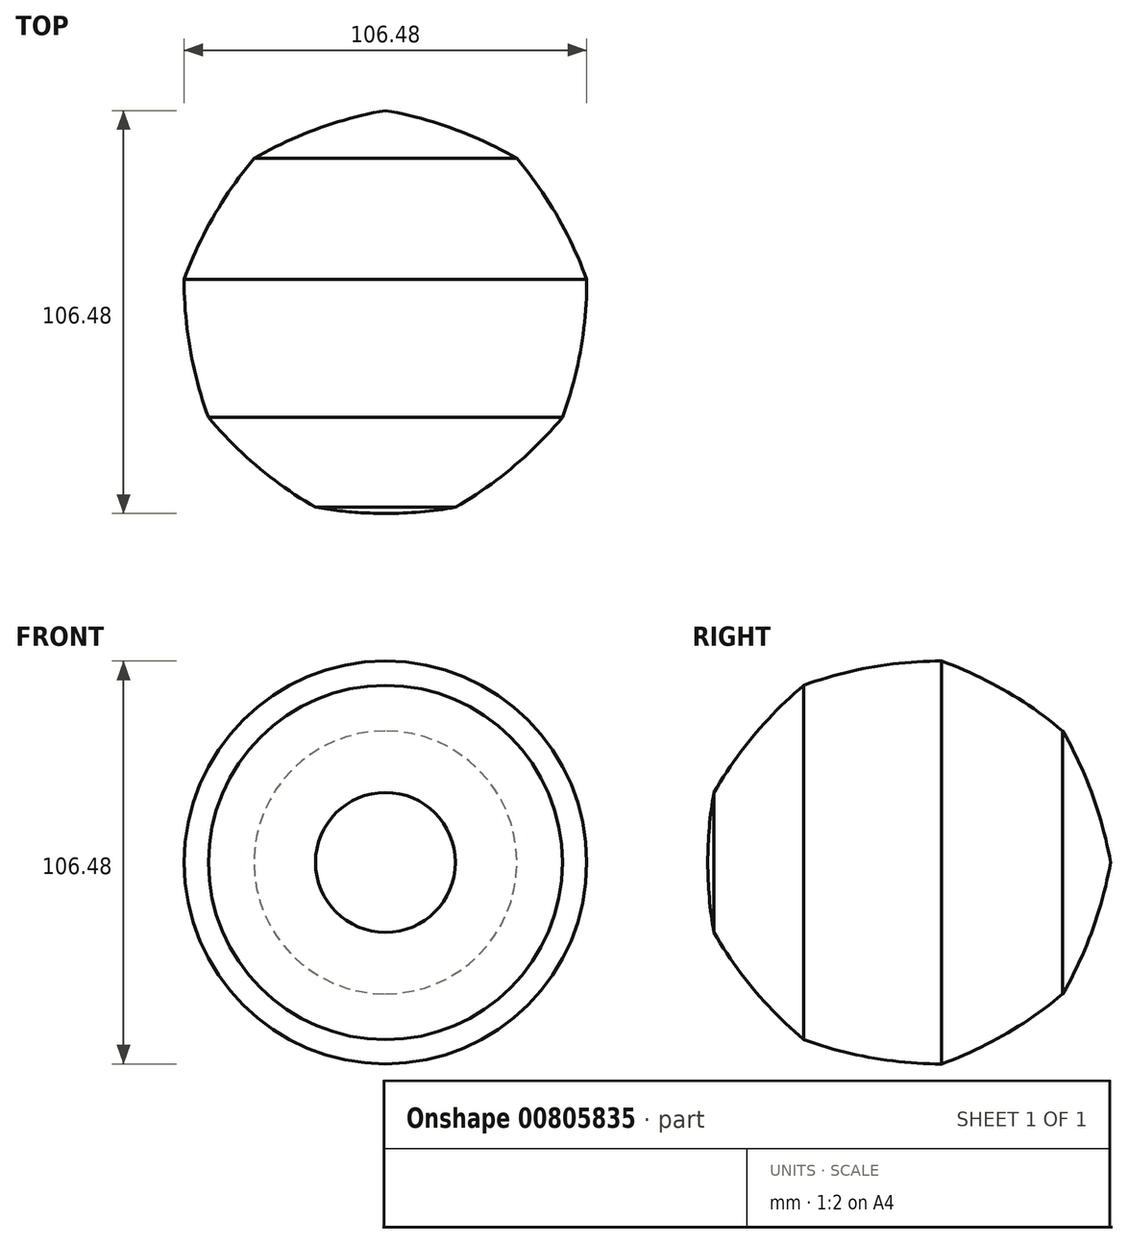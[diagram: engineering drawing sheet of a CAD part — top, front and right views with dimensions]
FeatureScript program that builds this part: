
annotation { "Feature Type Name" : "Feature", "Feature Type Description" : "" }
export const myFeature = defineFeature(function(context is Context, id is Id, definition is map)
    precondition{}
    {
        {
            var Q0;
            Q0=qCreatedBy(makeId("Top.planeOp"),FACE);
            var sketch = newSketch(context, id + "F0", { "sketchPlane" : qUnion([Q0])});
            skCircle(sketch, "E0.cCircle", {"center": v(0, 0) * mm, "radius": 50.8 * mm, "construction": true});
            skLineSegment(sketch, "E0.0", {"start": v(34.75, 41.41) * mm, "end": v(53.24, 9.39) * mm});
            skLineSegment(sketch, "E0.1", {"start": v(53.24, 9.39) * mm, "end": v(46.82, -27.03) * mm});
            skLineSegment(sketch, "E0.2", {"start": v(46.82, -27.03) * mm, "end": v(18.49, -50.8) * mm});
            skLineSegment(sketch, "E0.3", {"start": v(18.49, -50.8) * mm, "end": v(-18.49, -50.8) * mm});
            skLineSegment(sketch, "E0.4", {"start": v(-18.49, -50.8) * mm, "end": v(-46.82, -27.03) * mm});
            skLineSegment(sketch, "E0.5", {"start": v(-46.82, -27.03) * mm, "end": v(-53.24, 9.39) * mm});
            skLineSegment(sketch, "E0.6", {"start": v(-53.24, 9.39) * mm, "end": v(-34.75, 41.41) * mm});
            skLineSegment(sketch, "E0.7", {"start": v(-34.75, 41.41) * mm, "end": v(0, 54.06) * mm});
            skLineSegment(sketch, "E0.8", {"start": v(0, 54.06) * mm, "end": v(34.75, 41.41) * mm});
            skPoint(sketch, "E0.0.midPoint", {"position": v(44, 25.4) * mm});
            skCircle(sketch, "E1", {"center": v(0, 54.06) * mm, "radius": 106.48 * mm});
            skCircle(sketch, "E2", {"center": v(-34.75, 41.41) * mm, "radius": 106.48 * mm});
            skCircle(sketch, "E3", {"center": v(-53.24, 9.39) * mm, "radius": 106.48 * mm});
            skCircle(sketch, "E4", {"center": v(-46.82, -27.03) * mm, "radius": 106.48 * mm});
            skCircle(sketch, "E5", {"center": v(-18.49, -50.8) * mm, "radius": 106.48 * mm});
            skCircle(sketch, "E6", {"center": v(18.49, -50.8) * mm, "radius": 106.48 * mm});
            skCircle(sketch, "E7", {"center": v(46.82, -27.03) * mm, "radius": 106.48 * mm});
            skCircle(sketch, "E8", {"center": v(53.24, 9.39) * mm, "radius": 106.48 * mm});
            skCircle(sketch, "E9", {"center": v(34.75, 41.41) * mm, "radius": 106.48 * mm});
            skLineSegment(sketch, "E10", {"start": v(0, 76.2) * mm, "end": v(0, -76.2) * mm});
            skSolve(sketch);
        }
        {
            var Q0;
            {var subQ0=sQuery(id+"F0.wireOp",EDGE,"E0.4");Q0=makeQuery(id+"F0.imprint","IMPRINT",FACE,{"disambiguationData":[TD([[makeQuery(id+"F0.imprint","IMPRINT",EDGE,{"derivedFrom":subQ0}),-1.0]])]});}
            var Q1;
            {var subQ0=sQuery(id+"F0.wireOp",EDGE,"E0.5");Q1=makeQuery(id+"F0.imprint","IMPRINT",FACE,{"disambiguationData":[TD([[makeQuery(id+"F0.imprint","IMPRINT",EDGE,{"derivedFrom":subQ0}),1.0]])]});}
            var Q2;
            {var subQ0=sQuery(id+"F0.wireOp",EDGE,"E0.7");Q2=makeQuery(id+"F0.imprint","IMPRINT",FACE,{"disambiguationData":[TD([[makeQuery(id+"F0.imprint","IMPRINT",EDGE,{"derivedFrom":subQ0}),1.0]])]});}
            var Q3;
            {var subQ0=sQuery(id+"F0.wireOp",EDGE,"E0.6");Q3=makeQuery(id+"F0.imprint","IMPRINT",FACE,{"disambiguationData":[TD([[makeQuery(id+"F0.imprint","IMPRINT",EDGE,{"derivedFrom":subQ0}),1.0]])]});}
            var Q4;
            {var subQ0=sQuery(id+"F0.wireOp",EDGE,"E0.4");Q4=makeQuery(id+"F0.imprint","IMPRINT",FACE,{"disambiguationData":[TD([[makeQuery(id+"F0.imprint","IMPRINT",EDGE,{"derivedFrom":subQ0}),1.0]])]});}
            var Q5;
            {var subQ1=sQuery(id+"F0.wireOp",EDGE,"E0.3");var subQ3=sQuery(id+"F0.wireOp",EDGE,"E10");var subQ4=makeQuery(id+"F0.imprint","INTERSECT",VERTEX,{"derivedFrom":[subQ1,subQ3]});Q5=makeQuery(id+"F0.imprint","IMPRINT",FACE,{"disambiguationData":[TD([[makeQuery(id+"F0.imprint","IMPRINT",EDGE,{"disambiguationData":[TD([[subQ4,-1.0]])],"derivedFrom":subQ3}),-1.0]])]});}
            var Q6;
            Q6=sQuery(id+"F0.wireOp",EDGE,"E10");
            revolve(context, id + "F1", {"surfaceOperationType" : NewSurfaceOperationType.NEW, "entities" : qUnion([Q0, Q1, Q2, Q3, Q4, Q5]), "axis" : qUnion([Q6]), "revolveType" : RevolveType.FULL});
        }
    });
